# Revit family: Access_Door_ACUDOR_FireRated_Drywall_FW-5015
name_source: partatom
category: Doors
revit_build: Autodesk Revit 2017 (Build: 20171027_0315(x64)
units: mm (PartAtom-declared; Revit-internal decimal feet)

## family parameters
Cut with Voids When Loaded = No
Host = Face
Room Calculation Point = No
Shared = No

## types (6) — shared parameters
Analytic Construction = <None>
Default Elevation = 48 "
Description = RECESSED FOR DRYWALL
Manufacturer = ACUDOR
Material Finish = Metal - Acudor - Stainless - Polished
URL = www.acudor.com
zero-valued in all types: Thickness

## per-type parameters (varying)
| type | Code | Height | Wall Offset | Width |
| FW-5015-1212 | 1 | 14.48 " | 0.5 " | 14.48 " |
| FW-5015-1414 | 2 | 16.48 " | 0 " | 16.48 " |
| FW-5015-1818 | 4 | 20.48 " | 0 " | 20.48 " |
| FW-5015-2424 | 5 | 26.48 " | 0 " | 26.48 " |
| FW-5015-2436 | 6 | 38.48 " | 0 " | 26.48 " |
| FW-5015-1616 | 3 | 18.48 " | 0 " | 18.48 " |

note: column(s) folded — value = type name in every type: Model

## geometry (parser evidence)
native form markers: Blend x2, Sweep x10
no freeform markers — native parametric forms only
